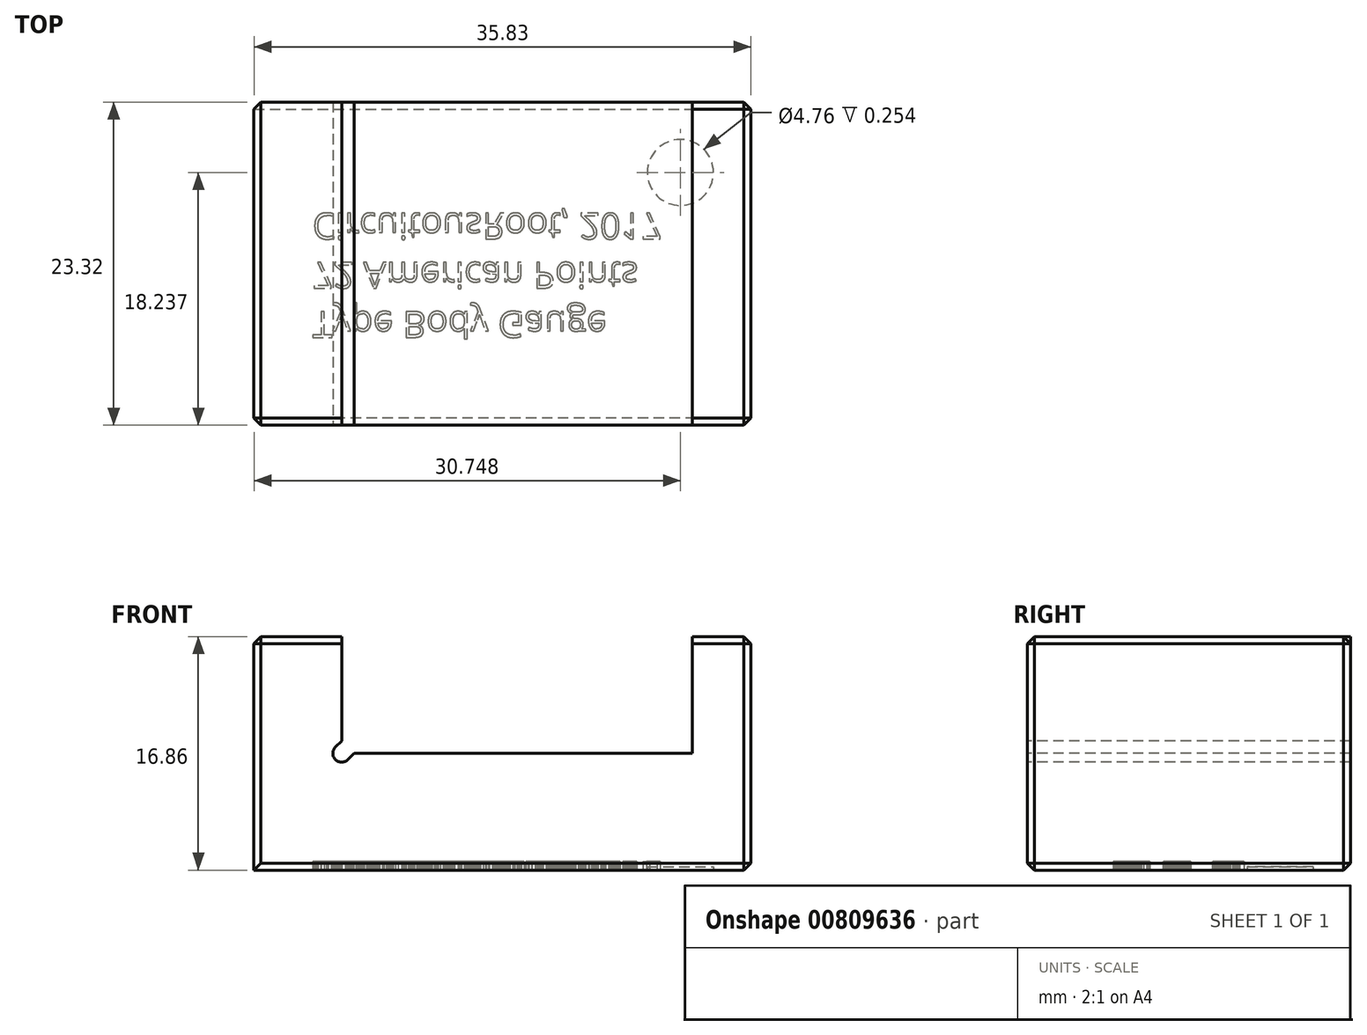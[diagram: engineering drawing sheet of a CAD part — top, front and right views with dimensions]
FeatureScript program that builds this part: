
annotation { "Feature Type Name" : "Feature", "Feature Type Description" : "" }
export const myFeature = defineFeature(function(context is Context, id is Id, definition is map)
    precondition{}
    {
        {
            assignVariable(context, id + "F0", {"variableType" : VariableType.LENGTH, "name" : "PointsInInches", "lengthValue" : 0.35 * mm});
        }
        {
            var Q0;
            Q0=qCreatedBy(makeId("Top.planeOp"),FACE);
            var sketch = newSketch(context, id + "F1", { "sketchPlane" : qUnion([Q0])});
            skLineSegment(sketch, "E0.bottom", {"start": v(0, 0) * mm, "end": v(25.3, 0) * mm});
            skLineSegment(sketch, "E0.top", {"start": v(0, 23.32) * mm, "end": v(25.3, 23.32) * mm});
            skLineSegment(sketch, "E0.left", {"start": v(0, 0) * mm, "end": v(0, 23.32) * mm});
            skLineSegment(sketch, "E0.right", {"start": v(25.3, 0) * mm, "end": v(25.3, 23.32) * mm});
            skSolve(sketch);
        }
        {
            var Q0;
            Q0 = qSketchRegion(id + "F1", true);
            extrude(context, id + "F2", {"entities" : qUnion([Q0]), "oppositeDirection" : true, "depth" : 24 * getVariable(context, 'PointsInInches'), "offsetDistance" : 25.4 * mm});
        }
        {
            var Q0;
            Q0=makeQuery(id+"F2.opExtrude","SWEPT_FACE",FACE,{"disambiguationData":[OSD([sQuery(id+"F1.wireOp",EDGE,"E0.left")])]});
            var sketch = newSketch(context, id + "F3", { "sketchPlane" : qUnion([Q0])});
            skLineSegment(sketch, "E1.bottom", {"start": v(-23.32, -8.43) * mm, "end": v(0, -8.43) * mm});
            skLineSegment(sketch, "E1.top", {"start": v(-23.32, 8.43) * mm, "end": v(0, 8.43) * mm});
            skLineSegment(sketch, "E1.left", {"start": v(-23.32, -8.43) * mm, "end": v(-23.32, 8.43) * mm});
            skLineSegment(sketch, "E1.right", {"start": v(0, -8.43) * mm, "end": v(0, 8.43) * mm});
            skSolve(sketch);
        }
        {
            var Q0;
            Q0 = qSketchRegion(id + "F3", true);
            extrude(context, id + "F4", {"entities" : qUnion([Q0]), "operationType" : NewBodyOperationType.ADD, "depth" : 18 * getVariable(context, 'PointsInInches'), "offsetDistance" : 25.4 * mm});
        }
        {
            var Q0;
            Q0=makeQuery(id+"F2.opExtrude","SWEPT_FACE",FACE,{"disambiguationData":[OSD([sQuery(id+"F1.wireOp",EDGE,"E0.right")])]});
            var sketch = newSketch(context, id + "F5", { "sketchPlane" : qUnion([Q0])});
            skLineSegment(sketch, "E2.bottom", {"start": v(0, -8.43) * mm, "end": v(23.32, -8.43) * mm});
            skLineSegment(sketch, "E2.top", {"start": v(0, 8.43) * mm, "end": v(23.32, 8.43) * mm});
            skLineSegment(sketch, "E2.left", {"start": v(0, -8.43) * mm, "end": v(0, 8.43) * mm});
            skLineSegment(sketch, "E2.right", {"start": v(23.32, -8.43) * mm, "end": v(23.32, 8.43) * mm});
            skSolve(sketch);
        }
        {
            var Q0;
            Q0 = qSketchRegion(id + "F5", true);
            extrude(context, id + "F6", {"entities" : qUnion([Q0]), "operationType" : NewBodyOperationType.ADD, "depth" : 12 * getVariable(context, 'PointsInInches'), "offsetDistance" : 25.4 * mm});
        }
        {
            var Q0;
            Q0=makeQuery(id+"F4.opExtrude","CAP_FACE",FACE,{"disambiguationData":[OSD([sQuery(id+"F3.wireOp",EDGE,"E1.bottom"),sQuery(id+"F3.wireOp",EDGE,"E1.top"),sQuery(id+"F3.wireOp",EDGE,"E1.left"),sQuery(id+"F3.wireOp",EDGE,"E1.right")])],"isStart":true});
            cPlane(context, id + "F7", {"entities" : qUnion([Q0]), "cplaneType" : CPlaneType.OFFSET, "offset" : (72 * getVariable(context, 'PointsInInches')) / 2, "width" : 152.4 * mm, "height" : 152.4 * mm});
        }
        {
            var Q0;
            Q0=makeQuery(id+"F2.opExtrude","CAP_FACE",FACE,{"disambiguationData":[OSD([sQuery(id+"F1.wireOp",EDGE,"E0.bottom"),sQuery(id+"F1.wireOp",EDGE,"E0.top"),sQuery(id+"F1.wireOp",EDGE,"E0.left"),sQuery(id+"F1.wireOp",EDGE,"E0.right")])],"isStart":false});
            var sketch = newSketch(context, id + "F8", { "sketchPlane" : qUnion([Q0])});
            skText(sketch, "E3", { "text": "Type Body Gauge\n72 American Points\nCircuitousRoot, 2017", "fontName": "OpenSans-Regular.ttf"});
            const initialGuessF8  = {"E3": [-0.0021, -0.0082, 1, 0, 0.00188]};
            skSetInitialGuess(sketch, initialGuessF8);
            skSolve(sketch);
        }
        {
            var Q0;
            Q0 = qSketchRegion(id + "F8", true);
            extrude(context, id + "F9", {"entities" : qUnion([Q0]), "operationType" : NewBodyOperationType.REMOVE, "oppositeDirection" : true, "depth" : 0.64 * mm, "offsetDistance" : 25.4 * mm});
        }
        {
            var Q0;
            {var subQ0=sQuery(id+"F1.wireOp",EDGE,"E0.bottom");var subQ1=sQuery(id+"F1.wireOp",EDGE,"E0.top");var subQ4=sQuery(id+"F3.wireOp",EDGE,"E1.bottom");var subQ7=sQuery(id+"F5.wireOp",EDGE,"E2.bottom");Q0=makeQuery(id+"F9.boolean.opBoolean","SPLIT",FACE,{"disambiguationData":[TD([makeQuery(id+"F2.opExtrude","SWEPT_FACE",FACE,{"disambiguationData":[OSD([subQ0])]})])],"derivedFrom":makeQuery(id+"F6.boolean.opBoolean","MERGE",FACE,{"derivedFrom":[makeQuery(id+"F4.boolean.opBoolean","MERGE",FACE,{"derivedFrom":[makeQuery(id+"F2.opExtrude","CAP_FACE",FACE,{"disambiguationData":[OSD([subQ0,subQ1,sQuery(id+"F1.wireOp",EDGE,"E0.left"),sQuery(id+"F1.wireOp",EDGE,"E0.right")])],"isStart":false}),makeQuery(id+"F4.opExtrude","SWEPT_FACE",FACE,{"disambiguationData":[OSD([subQ4])]})]}),makeQuery(id+"F6.opExtrude","SWEPT_FACE",FACE,{"disambiguationData":[OSD([subQ7])]})]})});}
            var sketch = newSketch(context, id + "F10", { "sketchPlane" : qUnion([Q0])});
            skCircle(sketch, "E4", {"center": v(24.43, -18.24) * mm, "radius": 2.38 * mm});
            skSolve(sketch);
        }
        {
            var Q0;
            Q0 = qSketchRegion(id + "F10", true);
            extrude(context, id + "F11", {"entities" : qUnion([Q0]), "operationType" : NewBodyOperationType.REMOVE, "oppositeDirection" : true, "depth" : 0.25 * mm, "offsetDistance" : 25.4 * mm});
        }
        {
            var Q0;
            Q0=makeQuery(id+"F4.opExtrude","CAP_EDGE",EDGE,{"disambiguationData":[OSD([sQuery(id+"F3.wireOp",EDGE,"E1.top")])],"isStart":false});
            var Q1;
            Q1=makeQuery(id+"F6.opExtrude","CAP_EDGE",EDGE,{"disambiguationData":[OSD([sQuery(id+"F5.wireOp",EDGE,"E2.top")])],"isStart":false});
            var Q2;
            Q2=makeQuery(id+"F4.opExtrude","CAP_EDGE",EDGE,{"disambiguationData":[OSD([sQuery(id+"F3.wireOp",EDGE,"E1.right")])],"isStart":false});
            var Q3;
            Q3=makeQuery(id+"F4.opExtrude","CAP_EDGE",EDGE,{"disambiguationData":[OSD([sQuery(id+"F3.wireOp",EDGE,"E1.left")])],"isStart":false});
            var Q4;
            Q4=makeQuery(id+"F4.opExtrude","SWEPT_EDGE",EDGE,{"disambiguationData":[OSD([sQuery(id+"F3.wireOp",EDGE,"E1.top"),sQuery(id+"F3.wireOp",EDGE,"E1.right")])]});
            var Q5;
            Q5=makeQuery(id+"F4.opExtrude","SWEPT_EDGE",EDGE,{"disambiguationData":[OSD([sQuery(id+"F3.wireOp",EDGE,"E1.bottom"),sQuery(id+"F3.wireOp",EDGE,"E1.right")])]});
            var Q6;
            Q6=makeQuery(id+"F2.opExtrude","CAP_EDGE",EDGE,{"disambiguationData":[OSD([sQuery(id+"F1.wireOp",EDGE,"E0.bottom")])],"isStart":false});
            var Q7;
            Q7=makeQuery(id+"F6.opExtrude","SWEPT_EDGE",EDGE,{"disambiguationData":[OSD([sQuery(id+"F5.wireOp",EDGE,"E2.bottom"),sQuery(id+"F5.wireOp",EDGE,"E2.right")])]});
            var Q8;
            Q8=makeQuery(id+"F2.opExtrude","CAP_EDGE",EDGE,{"disambiguationData":[OSD([sQuery(id+"F1.wireOp",EDGE,"E0.top")])],"isStart":false});
            var Q9;
            Q9=makeQuery(id+"F4.opExtrude","SWEPT_EDGE",EDGE,{"disambiguationData":[OSD([sQuery(id+"F3.wireOp",EDGE,"E1.bottom"),sQuery(id+"F3.wireOp",EDGE,"E1.left")])]});
            var Q10;
            Q10=makeQuery(id+"F6.opExtrude","SWEPT_EDGE",EDGE,{"disambiguationData":[OSD([sQuery(id+"F5.wireOp",EDGE,"E2.top"),sQuery(id+"F5.wireOp",EDGE,"E2.left")])]});
            var Q11;
            Q11=makeQuery(id+"F6.opExtrude","CAP_EDGE",EDGE,{"disambiguationData":[OSD([sQuery(id+"F5.wireOp",EDGE,"E2.left")])],"isStart":false});
            var Q12;
            Q12=makeQuery(id+"F6.opExtrude","CAP_EDGE",EDGE,{"disambiguationData":[OSD([sQuery(id+"F5.wireOp",EDGE,"E2.bottom")])],"isStart":false});
            var Q13;
            Q13=makeQuery(id+"F6.opExtrude","CAP_EDGE",EDGE,{"disambiguationData":[OSD([sQuery(id+"F5.wireOp",EDGE,"E2.right")])],"isStart":false});
            var Q14;
            Q14=makeQuery(id+"F6.opExtrude","SWEPT_EDGE",EDGE,{"disambiguationData":[OSD([sQuery(id+"F5.wireOp",EDGE,"E2.top"),sQuery(id+"F5.wireOp",EDGE,"E2.right")])]});
            var Q15;
            Q15=makeQuery(id+"F6.opExtrude","SWEPT_EDGE",EDGE,{"disambiguationData":[OSD([sQuery(id+"F5.wireOp",EDGE,"E2.bottom"),sQuery(id+"F5.wireOp",EDGE,"E2.left")])]});
            chamfer(context, id + "F12", {"entities" : qUnion([Q0, Q1, Q2, Q3, Q4, Q5, Q6, Q7, Q8, Q9, Q10, Q11, Q12, Q13, Q14, Q15]), "width" : 0.5 * mm, "tangentPropagation" : true});
        }
        {
            var Q0;
            Q0=makeQuery(id+"F6.boolean.opBoolean","MERGE",FACE,{"derivedFrom":[makeQuery(id+"F4.boolean.opBoolean","MERGE",FACE,{"derivedFrom":[makeQuery(id+"F2.opExtrude","SWEPT_FACE",FACE,{"disambiguationData":[OSD([sQuery(id+"F1.wireOp",EDGE,"E0.bottom")])]}),makeQuery(id+"F4.opExtrude","SWEPT_FACE",FACE,{"disambiguationData":[OSD([sQuery(id+"F3.wireOp",EDGE,"E1.right")])]})]}),makeQuery(id+"F6.opExtrude","SWEPT_FACE",FACE,{"disambiguationData":[OSD([sQuery(id+"F5.wireOp",EDGE,"E2.left")])]})]});
            var sketch = newSketch(context, id + "F13", { "sketchPlane" : qUnion([Q0])});
            skLineSegment(sketch, "E5", {"start": v(0, 0) * mm, "end": v(-2.64, -2.64) * mm, "construction": true});
            skLineSegment(sketch, "E6", {"start": v(-0.45, 0.45) * mm, "end": v(0, 0.9) * mm});
            skLineSegment(sketch, "E7", {"start": v(0.45, -0.45) * mm, "end": v(0.9, 0) * mm});
            skArc(sketch, "E8", {"start": v(-0.45, 0.45) * mm, "mid": v(-0.45, -0.45) * mm, "end": v(0.45, -0.45) * mm});
            skLineSegment(sketch, "E9.0", {"start": v(0, 0) * mm, "end": v(0, 7.92) * mm});
            skLineSegment(sketch, "E10.0", {"start": v(0, 0) * mm, "end": v(25.3, 0) * mm});
            skLineSegment(sketch, "E11", {"start": v(0, 0.9) * mm, "end": v(0.9, 0) * mm});
            skSolve(sketch);
        }
        {
            var Q0;
            Q0 = qSketchRegion(id + "F13", true);
            extrude(context, id + "F14", {"entities" : qUnion([Q0]), "operationType" : NewBodyOperationType.REMOVE, "endBound" : BoundingType.THROUGH_ALL, "oppositeDirection" : true, "depth" : 25.4 * mm, "offsetDistance" : 25.4 * mm});
        }
    });
